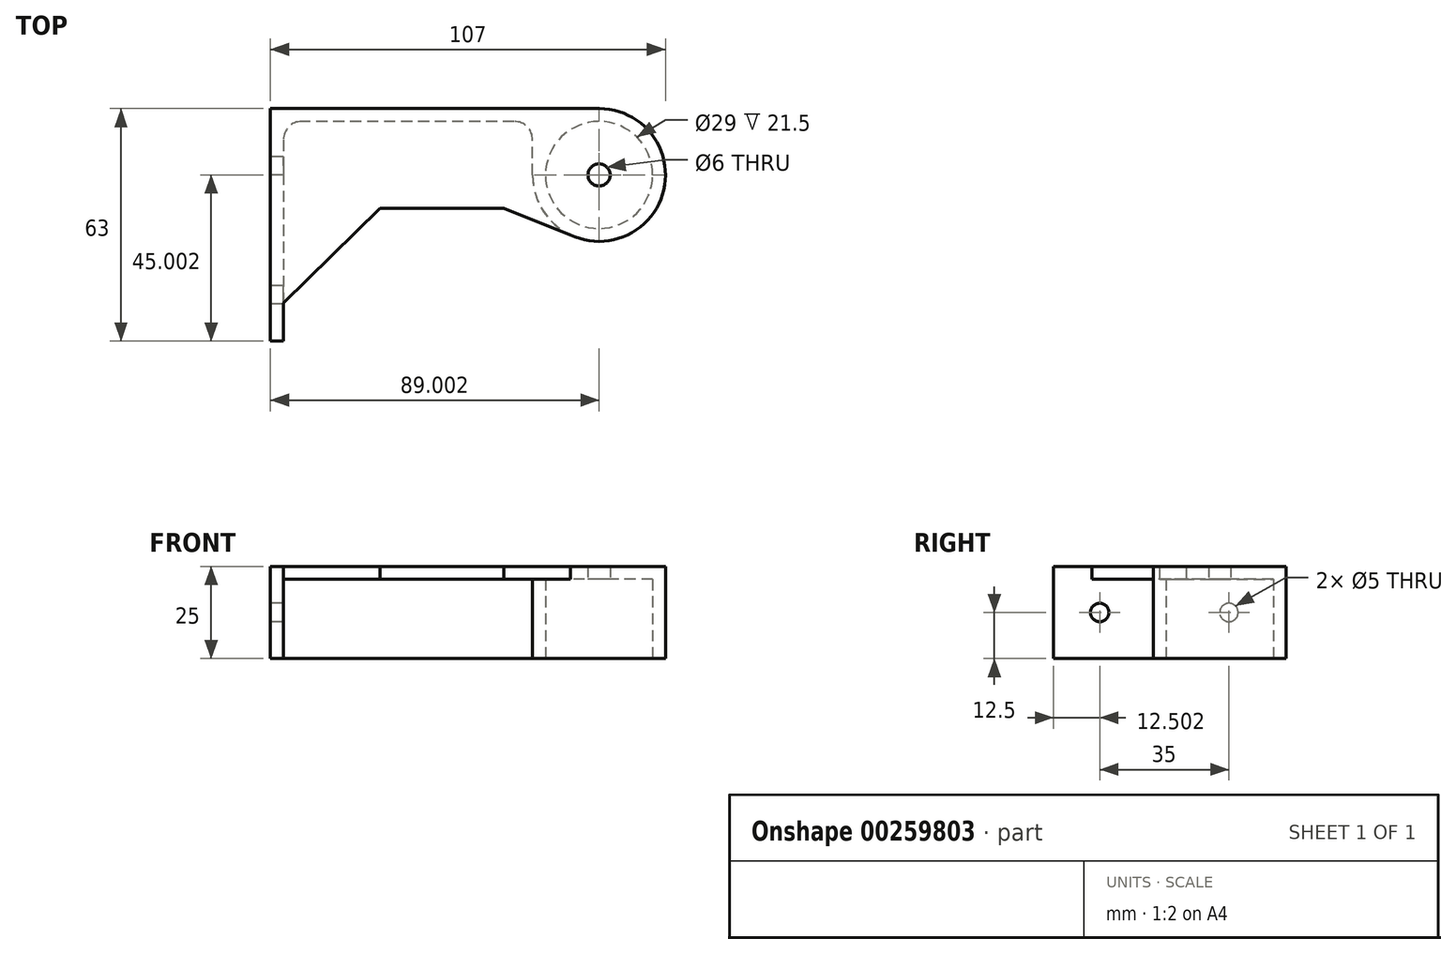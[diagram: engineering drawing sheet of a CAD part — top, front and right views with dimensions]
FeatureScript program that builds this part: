
annotation { "Feature Type Name" : "Feature", "Feature Type Description" : "" }
export const myFeature = defineFeature(function(context is Context, id is Id, definition is map)
    precondition{}
    {
        {
            var Q0;
            Q0=qCreatedBy(makeId("Top.planeOp"),FACE);
            var sketch = newSketch(context, id + "F0", { "sketchPlane" : qUnion([Q0])});
            skLineSegment(sketch, "E0", {"start": v(-44.26, -25.47) * mm, "end": v(-44.26, 24.53) * mm});
            skCircle(sketch, "E1", {"center": v(44.74, 19.53) * mm, "radius": 3 * mm});
            skLineSegment(sketch, "E2", {"start": v(18.42, 19.53) * mm, "end": v(70.29, 19.53) * mm, "construction": true});
            skLineSegment(sketch, "E3", {"start": v(-40.76, 34.03) * mm, "end": v(-40.76, -25.47) * mm});
            skPoint(sketch, "E4.orphan", {"position": v(26.74, 24.53) * mm});
            skLineSegment(sketch, "E5", {"start": v(-44.26, -25.47) * mm, "end": v(-40.76, -25.47) * mm});
            skPoint(sketch, "E6.start.orphan", {"position": v(26.74, 19.53) * mm});
            skArc(sketch, "E7", {"start": v(26.74, 19.53) * mm, "mid": v(57.5, 6.83) * mm, "end": v(44.67, 37.53) * mm});
            skCircle(sketch, "E8", {"center": v(44.74, 19.53) * mm, "radius": 14.5 * mm});
            skPoint(sketch, "E9.orphan", {"position": v(26.74, 22.03) * mm});
            skLineSegment(sketch, "E10", {"start": v(-44.26, 24.53) * mm, "end": v(-44.26, 37.53) * mm});
            skLineSegment(sketch, "E11", {"start": v(44.81, 37.53) * mm, "end": v(-44.26, 37.53) * mm});
            skLineSegment(sketch, "E12", {"start": v(26.74, 19.53) * mm, "end": v(26.74, 34.03) * mm});
            skLineSegment(sketch, "E13", {"start": v(26.74, 34.03) * mm, "end": v(-40.76, 34.03) * mm});
            skSolve(sketch);
        }
        {
            var Q0;
            {var subQ3=sQuery(id+"F0.wireOp",EDGE,"E0");Q0=makeQuery(id+"F0.imprint","IMPRINT",FACE,{"disambiguationData":[TD([[makeQuery(id+"F0.imprint","IMPRINT",EDGE,{"derivedFrom":subQ3}),-1.0]])]});}
            extrude(context, id + "F1", {"entities" : qUnion([Q0]), "depth" : 25 * mm, "offsetDistance" : 25 * mm});
        }
        {
            var Q0;
            Q0=makeQuery(id+"F1.opExtrude","CAP_FACE",FACE,{"disambiguationData":[OSD([sQuery(id+"F0.wireOp",EDGE,"E0"),sQuery(id+"F0.wireOp",EDGE,"9EhYY78m-zoHk-iMrv-e83C-6VlNWBI4XpSo"),sQuery(id+"F0.wireOp",EDGE,"8QMgwL4l-eUgF-bXba-84mB-vObHb4zvUH5H"),sQuery(id+"F0.wireOp",EDGE,"E6"),sQuery(id+"F0.wireOp",EDGE,"3onknbom-nDR8-QG2M-WJFN-s93Y46cqOnpk"),sQuery(id+"F0.wireOp",EDGE,"P25SQ9gr-SBM6-nuFK-kGic-qiJolmAvlV25"),sQuery(id+"F0.wireOp",EDGE,"jLxib0JA-VgGV-74Fc-wNGU-5bSYWisP3I0S"),sQuery(id+"F0.wireOp",EDGE,"w1t1WZSq-hnDY-My2U-ti3M-12xU87QEO2nx"),sQuery(id+"F0.wireOp",EDGE,"BvRT03NC-QGzv-KDhi-lN9r-vG7JtMDw9sgh"),sQuery(id+"F0.wireOp",EDGE,"E3"),sQuery(id+"F0.wireOp",EDGE,"E5")])],"isStart":false});
            var sketch = newSketch(context, id + "F2", { "sketchPlane" : qUnion([Q0])});
            skPoint(sketch, "E14.visualSharp", {"position": v(21.09, 11.87) * mm});
            skPoint(sketch, "E15.visualSharp", {"position": v(-18, 11.87) * mm});
            skPoint(sketch, "E16.end.orphan", {"position": v(43.02, 0) * mm});
            skLineSegment(sketch, "E17", {"start": v(36.94, 3.31) * mm, "end": v(18.91, 10.56) * mm});
            skLineSegment(sketch, "E18", {"start": v(18.91, 10.56) * mm, "end": v(-14.57, 10.56) * mm});
            skLineSegment(sketch, "E19", {"start": v(-14.57, 10.56) * mm, "end": v(-40.76, -15.1) * mm});
            skSolve(sketch);
        }
        {
            var Q0;
            {var subQ7=sQuery(id+"F0.wireOp",EDGE,"E0");Q0=makeQuery(id+"F2.imprint","IMPRINT",FACE,{"disambiguationData":[TD([[makeQuery(id+"F2.imprint","IMPRINT",EDGE,{"derivedFrom":makeQuery(id+"F1.opExtrude","CAP_EDGE",EDGE,{"disambiguationData":[OSD([subQ7])],"isStart":false})}),-1.0]])]});}
            var Q1;
            {var subQ2=sQuery(id+"F2.wireOp",EDGE,"SgQ3EWNG-DneK-HrVH-vFpO-P6JwSViOGyTf");Q1=makeQuery(id+"F2.imprint","IMPRINT",FACE,{"disambiguationData":[TD([[makeQuery(id+"F2.imprint","IMPRINT",EDGE,{"derivedFrom":subQ2}),-1.0]])]});}
            var Q2;
            Q2=makeQuery(id+"F2.imprint","IMPRINT",FACE,{"disambiguationData":[TD([[makeQuery(id+"F2.imprint","IMPRINT",EDGE,{"derivedFrom":sQuery(id+"F2.wireOp",EDGE,"tCpqNb5R-hl54-qKNW-tL58-u9xZHlXqobxP")}),-1.0]])]});
            extrude(context, id + "F3", {"entities" : qUnion([Q0, Q1, Q2]), "operationType" : NewBodyOperationType.ADD, "oppositeDirection" : true, "depth" : 3 * mm, "offsetDistance" : 25 * mm});
        }
        {
            var Q0;
            Q0=makeQuery(id+"F1.opExtrude","SWEPT_FACE",FACE,{"disambiguationData":[OSD([sQuery(id+"F0.wireOp",EDGE,"E0")])]});
            var sketch = newSketch(context, id + "F4", { "sketchPlane" : qUnion([Q0])});
            skCircle(sketch, "E20", {"center": v(12.97, 12.5) * mm, "radius": 2.5 * mm});
            skCircle(sketch, "E21", {"center": v(-22.03, 12.5) * mm, "radius": 2.5 * mm});
            skCircle(sketch, "E22", {"center": v(-22.03, 12.5) * mm, "radius": 5 * mm});
            skSolve(sketch);
        }
        {
            var Q0;
            Q0=makeQuery(id+"F4.imprint","IMPRINT",FACE,{"disambiguationData":[TD([[makeQuery(id+"F4.imprint","IMPRINT",EDGE,{"derivedFrom":sQuery(id+"F4.wireOp",EDGE,"6Lwsdj9l-72Jd-1Nr0-Iw4I-RJKBA2kdM9Fr")}),1.0]])]});
            var Q1;
            Q1=makeQuery(id+"F4.imprint","IMPRINT",FACE,{"disambiguationData":[TD([[makeQuery(id+"F4.imprint","IMPRINT",EDGE,{"derivedFrom":sQuery(id+"F4.wireOp",EDGE,"E20")}),1.0]])]});
            var Q2;
            Q2=sQuery(id+"F4.wireOp",EDGE,"E20");
            var Q3;
            Q3=sQuery(id+"F4.wireOp",EDGE,"6Lwsdj9l-72Jd-1Nr0-Iw4I-RJKBA2kdM9Fr");
            extrude(context, id + "F5", {"entities" : qUnion([Q0, Q1]), "operationType" : NewBodyOperationType.REMOVE, "surfaceEntities" : qUnion([Q2, Q3]), "oppositeDirection" : true, "depth" : 25 * mm, "offsetDistance" : 25 * mm});
        }
        {
            var Q0;
            Q0=makeQuery(id+"F0.imprint","IMPRINT",FACE,{"disambiguationData":[TD([[makeQuery(id+"F0.imprint","IMPRINT",EDGE,{"derivedFrom":sQuery(id+"F0.wireOp",EDGE,"E1")}),1.0]])]});
            var Q1;
            Q1=sQuery(id+"F0.wireOp",EDGE,"E1");
            extrude(context, id + "F6", {"entities" : qUnion([Q0]), "operationType" : NewBodyOperationType.REMOVE, "surfaceEntities" : qUnion([Q1]), "depth" : 30 * mm, "offsetDistance" : 25 * mm});
        }
        {
            var Q0;
            Q0=makeQuery(id+"F1.opExtrude","SWEPT_FACE",FACE,{"disambiguationData":[OSD([sQuery(id+"F0.wireOp",EDGE,"E3")])]});
            var sketch = newSketch(context, id + "F7", { "sketchPlane" : qUnion([Q0])});
            skSolve(sketch);
        }
        {
            var Q0;
            Q0=makeQuery(id+"F4.imprint","IMPRINT",FACE,{"disambiguationData":[TD([[makeQuery(id+"F4.imprint","IMPRINT",EDGE,{"derivedFrom":sQuery(id+"F4.wireOp",EDGE,"E21")}),1.0]])]});
            var Q1;
            Q1=sQuery(id+"F4.wireOp",EDGE,"E21");
            extrude(context, id + "F8", {"entities" : qUnion([Q0]), "operationType" : NewBodyOperationType.REMOVE, "surfaceEntities" : qUnion([Q1]), "oppositeDirection" : true, "depth" : 25 * mm, "offsetDistance" : 25 * mm});
        }
        {
            var Q0;
            {var subQ3=sQuery(id+"F2.wireOp",EDGE,"E17");Q0=makeQuery(id+"F2.imprint","IMPRINT",FACE,{"disambiguationData":[TD([[makeQuery(id+"F2.imprint","IMPRINT",EDGE,{"derivedFrom":subQ3}),-1.0]])]});}
            var Q1;
            Q1=makeQuery(id+"F2.imprint","IMPRINT",FACE,{"disambiguationData":[TD([[makeQuery(id+"F2.imprint","IMPRINT",EDGE,{"derivedFrom":makeQuery(id+"F1.opExtrude","CAP_EDGE",EDGE,{"disambiguationData":[OSD([sQuery(id+"F0.wireOp",EDGE,"E8")])],"isStart":false})}),1.0]])]});
            extrude(context, id + "F9", {"entities" : qUnion([Q0, Q1]), "operationType" : NewBodyOperationType.ADD, "oppositeDirection" : true, "depth" : 3.5 * mm, "offsetDistance" : 25 * mm});
        }
        {
            var Q0;
            Q0=makeQuery(id+"F0.imprint","IMPRINT",FACE,{"disambiguationData":[TD([[makeQuery(id+"F0.imprint","IMPRINT",EDGE,{"derivedFrom":sQuery(id+"F0.wireOp",EDGE,"E1")}),1.0]])]});
            var Q1;
            Q1=sQuery(id+"F0.wireOp",EDGE,"E1");
            extrude(context, id + "F10", {"entities" : qUnion([Q0]), "operationType" : NewBodyOperationType.REMOVE, "surfaceEntities" : qUnion([Q1]), "depth" : 30 * mm, "offsetDistance" : 25 * mm});
        }
        {
            var Q0;
            Q0=makeQuery(id+"F1.opExtrude","SWEPT_EDGE",EDGE,{"disambiguationData":[OSD([sQuery(id+"F0.wireOp",EDGE,"E12"),sQuery(id+"F0.wireOp",EDGE,"E13")])]});
            var Q1;
            Q1=makeQuery(id+"F9.opExtrude","CAP_EDGE",EDGE,{"disambiguationData":[OSD([sQuery(id+"F0.wireOp",EDGE,"E12")])],"isStart":false});
            var Q2;
            Q2=makeQuery(id+"F9.opExtrude","CAP_EDGE",EDGE,{"disambiguationData":[OSD([sQuery(id+"F0.wireOp",EDGE,"E13")])],"isStart":false});
            var Q3;
            Q3=makeQuery(id+"F1.opExtrude","SWEPT_EDGE",EDGE,{"disambiguationData":[OSD([sQuery(id+"F0.wireOp",EDGE,"E3"),sQuery(id+"F0.wireOp",EDGE,"E13")])]});
            var Q4;
            Q4=makeQuery(id+"F9.opExtrude","CAP_EDGE",EDGE,{"disambiguationData":[OSD([sQuery(id+"F0.wireOp",EDGE,"E3")])],"isStart":false});
            fillet(context, id + "F11", {"entities" : qUnion([Q0, Q1, Q2, Q3, Q4]), "radius" : 5 * mm, "tangentPropagation" : true, "allowEdgeOverflow" : false});
        }
    });
